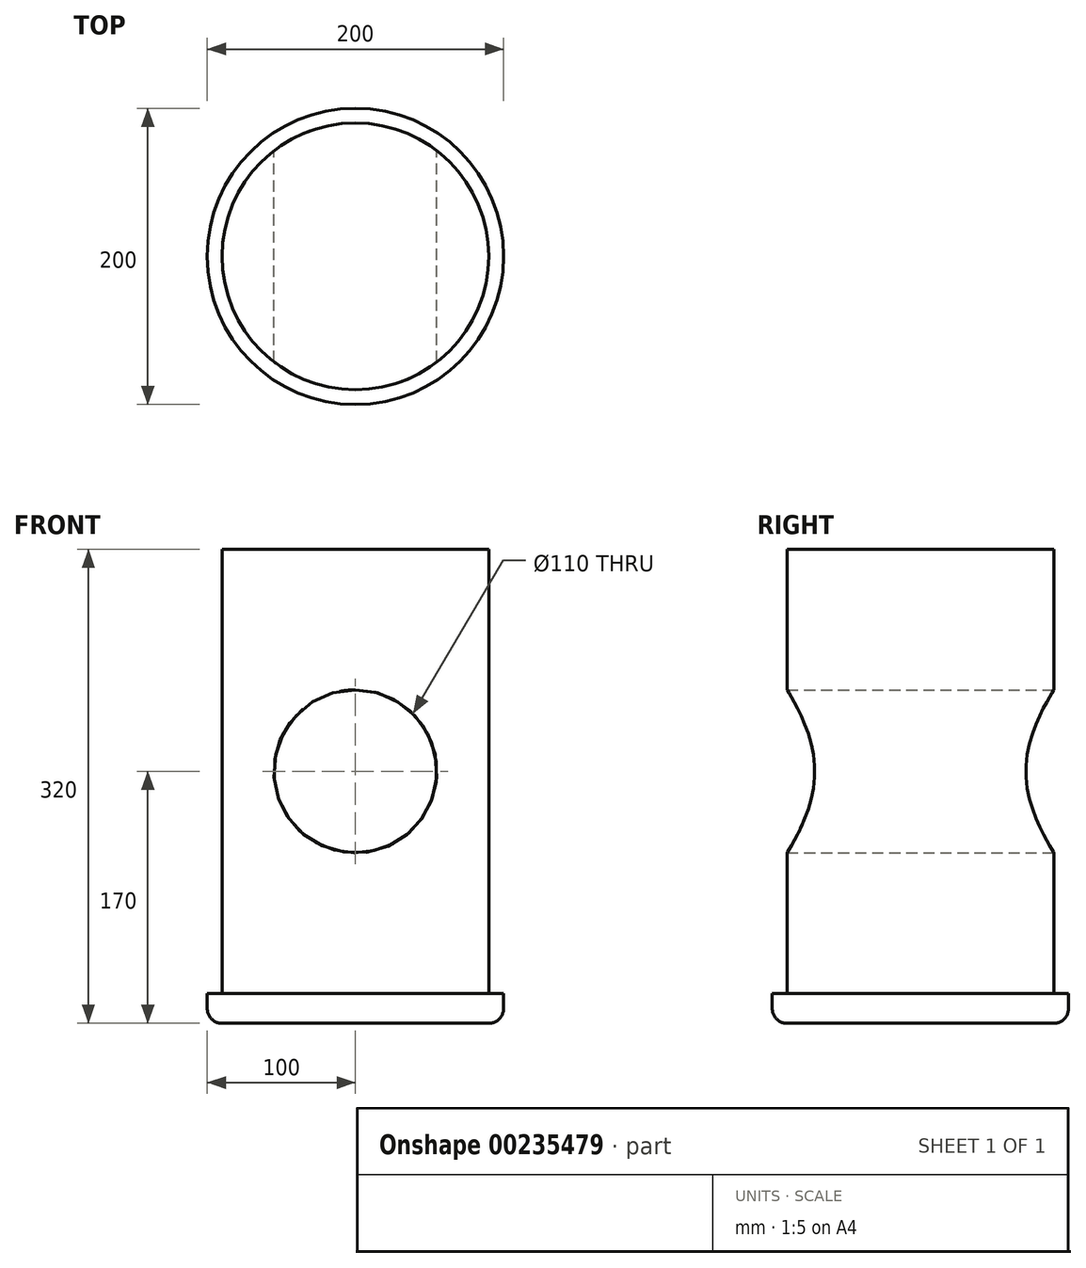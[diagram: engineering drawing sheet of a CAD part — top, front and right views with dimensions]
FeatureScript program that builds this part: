
annotation { "Feature Type Name" : "Feature", "Feature Type Description" : "" }
export const myFeature = defineFeature(function(context is Context, id is Id, definition is map)
    precondition{}
    {
        {
            var Q0;
            Q0=qCreatedBy(makeId("Top.planeOp"),FACE);
            var sketch = newSketch(context, id + "F0", { "sketchPlane" : qUnion([Q0])});
            skCircle(sketch, "E0", {"center": v(0, 0) * mm, "radius": 90 * mm});
            skCircle(sketch, "E1", {"center": v(0, 0) * mm, "radius": 100 * mm});
            skSolve(sketch);
        }
        {
            var Q0;
            Q0 = qSketchRegion(id + "F0", true);
            extrude(context, id + "F1", {"entities" : qUnion([Q0]), "depth" : 20 * mm});
        }
        {
            var Q0;
            Q0=makeQuery(id+"F0.imprint","IMPRINT",FACE,{"disambiguationData":[TD([[makeQuery(id+"F0.imprint","IMPRINT",EDGE,{"derivedFrom":sQuery(id+"F0.wireOp",EDGE,"E0")}),1.0]])]});
            extrude(context, id + "F2", {"entities" : qUnion([Q0]), "operationType" : NewBodyOperationType.ADD, "depth" : 320 * mm});
        }
        {
            var Q0;
            Q0=qCreatedBy(makeId("Front.planeOp"),FACE);
            var sketch = newSketch(context, id + "F3", { "sketchPlane" : qUnion([Q0])});
            skCircle(sketch, "E2", {"center": v(0, 170) * mm, "radius": 55 * mm});
            skSolve(sketch);
        }
        {
            var Q0;
            Q0 = qSketchRegion(id + "F3", true);
            extrude(context, id + "F4", {"entities" : qUnion([Q0]), "operationType" : NewBodyOperationType.REMOVE, "endBound" : BoundingType.SYMMETRIC, "depth" : 294 * mm});
        }
        {
            var Q0;
            Q0=makeQuery(id+"F1.opExtrude","CAP_EDGE",EDGE,{"disambiguationData":[OSD([sQuery(id+"F0.wireOp",EDGE,"E1")])],"isStart":true});
            fillet(context, id + "F5", {"entities" : qUnion([Q0]), "radius" : 10 * mm, "tangentPropagation" : true, "allowEdgeOverflow" : false});
        }
    });
